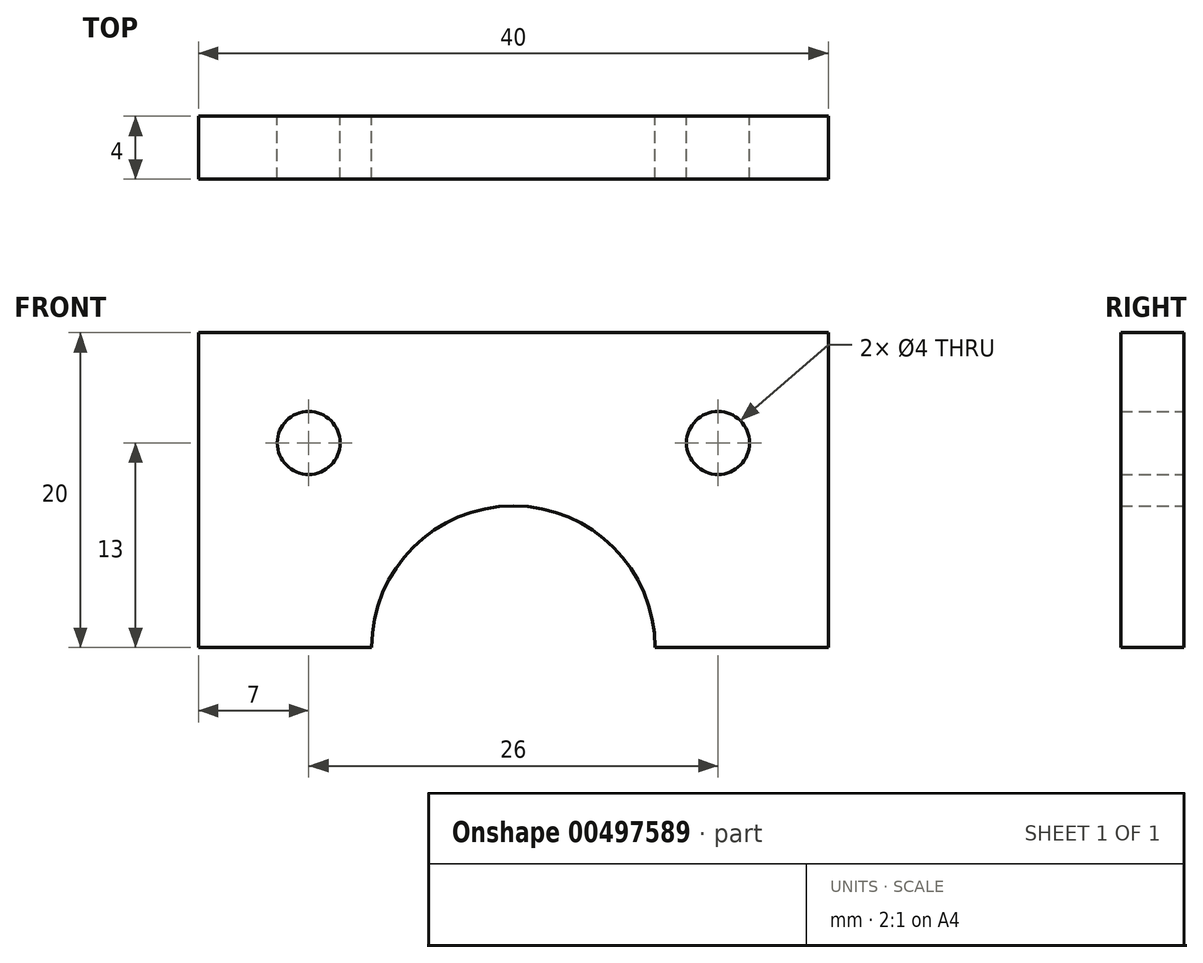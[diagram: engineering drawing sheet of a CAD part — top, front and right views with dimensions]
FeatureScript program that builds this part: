
annotation { "Feature Type Name" : "Feature", "Feature Type Description" : "" }
export const myFeature = defineFeature(function(context is Context, id is Id, definition is map)
    precondition{}
    {
        {
            var Q0;
            Q0=qCreatedBy(makeId("Front.planeOp"),FACE);
            var sketch = newSketch(context, id + "F0", { "sketchPlane" : qUnion([Q0])});
            skLineSegment(sketch, "E0.left", {"start": v(0, 20) * mm, "end": v(0, 0) * mm});
            skLineSegment(sketch, "E0.right", {"start": v(40, 20) * mm, "end": v(40, 0) * mm});
            skLineSegment(sketch, "E1", {"start": v(0, 20) * mm, "end": v(40, 20) * mm});
            skArc(sketch, "E2", {"start": v(29, 0) * mm, "mid": v(20, 9) * mm, "end": v(11, 0) * mm});
            skCircle(sketch, "E3", {"center": v(7, 13) * mm, "radius": 2 * mm});
            skCircle(sketch, "E4", {"center": v(33, 13) * mm, "radius": 2 * mm});
            skArc(sketch, "E5", {"start": v(31, 0) * mm, "mid": v(20, 11) * mm, "end": v(9, 0) * mm, "construction": true});
            skLineSegment(sketch, "E6", {"start": v(40, 0) * mm, "end": v(29, 0) * mm});
            skLineSegment(sketch, "E7.trimOffspring", {"start": v(11, 0) * mm, "end": v(0, 0) * mm});
            skPoint(sketch, "E8.orphan", {"position": v(0, 0) * mm});
            skSolve(sketch);
        }
        {
            var Q0;
            Q0=makeQuery(id+"F0.imprint","IMPRINT",FACE,{"disambiguationData":[TD([[makeQuery(id+"F0.imprint","IMPRINT",EDGE,{"derivedFrom":sQuery(id+"F0.wireOp",EDGE,"E0.left")}),1.0]])]});
            extrude(context, id + "F1", {"entities" : qUnion([Q0]), "depth" : 4 * mm});
        }
    });
